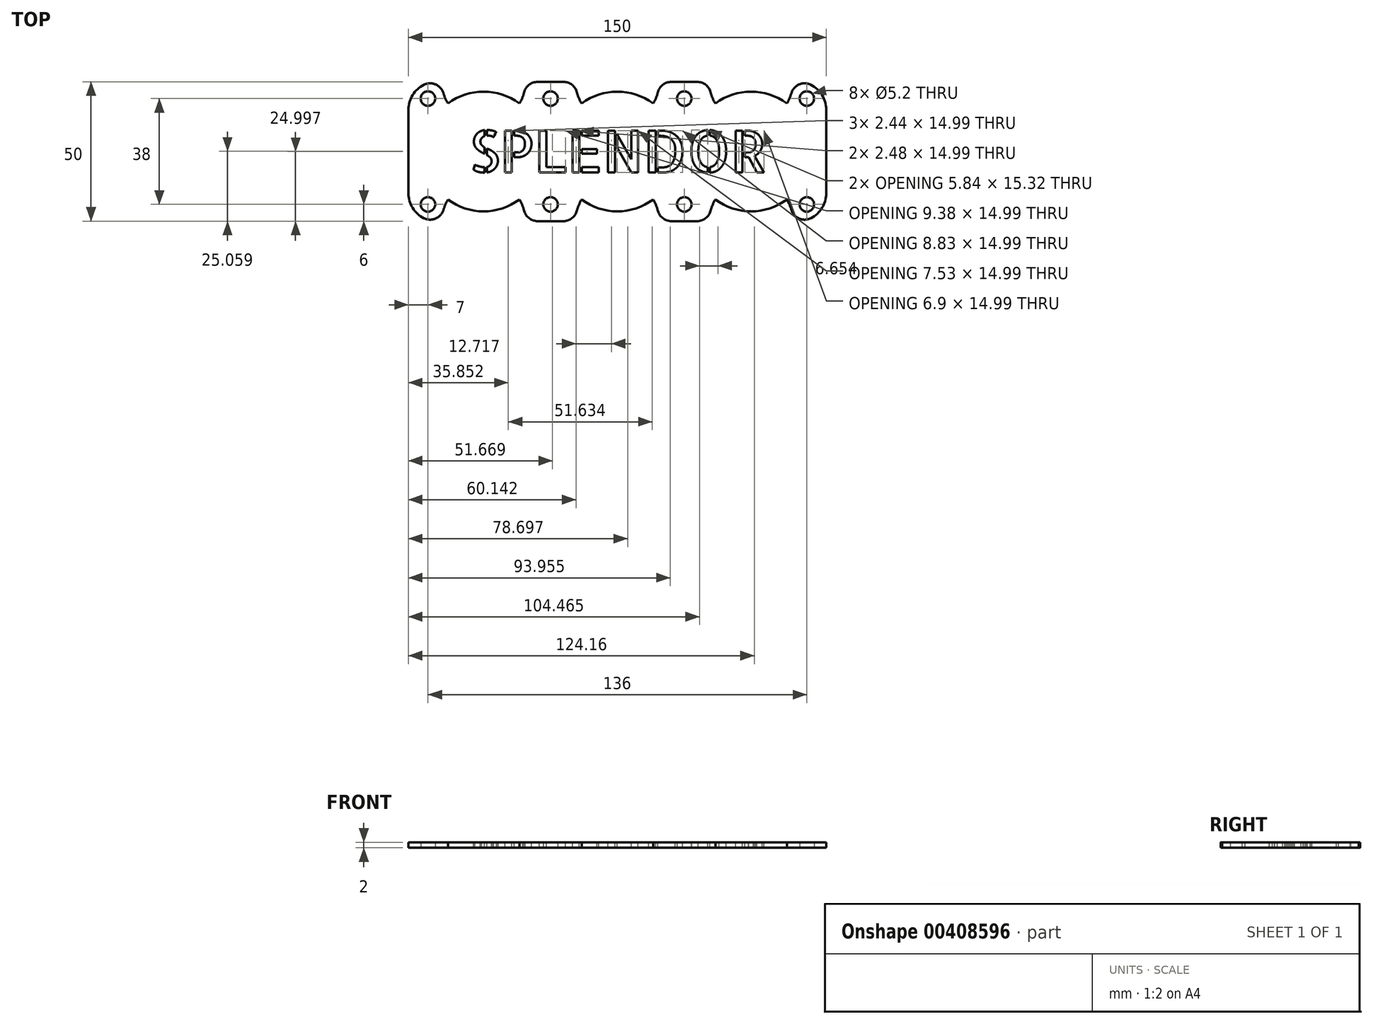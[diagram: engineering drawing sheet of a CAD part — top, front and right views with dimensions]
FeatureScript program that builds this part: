
annotation { "Feature Type Name" : "Feature", "Feature Type Description" : "" }
export const myFeature = defineFeature(function(context is Context, id is Id, definition is map)
    precondition{}
    {
        {
            var Q0;
            Q0=qCreatedBy(makeId("Top.planeOp"),FACE);
            var sketch = newSketch(context, id + "F0", { "sketchPlane" : qUnion([Q0])});
            skLineSegment(sketch, "E0.bottom", {"start": v(0, 0) * mm, "end": v(150, 0) * mm});
            skLineSegment(sketch, "E0.top", {"start": v(0, 50) * mm, "end": v(150, 50) * mm});
            skLineSegment(sketch, "E0.left", {"start": v(0, 0) * mm, "end": v(0, 50) * mm});
            skLineSegment(sketch, "E0.right", {"start": v(150, 0) * mm, "end": v(150, 50) * mm});
            skSolve(sketch);
        }
        {
            var Q0;
            Q0=makeQuery(id+"F0.imprint","IMPRINT",FACE,{"disambiguationData":[TD([[makeQuery(id+"F0.imprint","IMPRINT",EDGE,{"derivedFrom":sQuery(id+"F0.wireOp",EDGE,"E0.bottom")}),1.0]])]});
            var Q1;
            Q1=qSketchRegion(id+"F2",true);
            extrude(context, id + "F1", {"entities" : qUnion([Q0, Q1]), "depth" : 30 * mm});
        }
        {
            var Q0;
            Q0=makeQuery(id+"F1.opExtrude","CAP_FACE",FACE,{"disambiguationData":[OSD([sQuery(id+"F0.wireOp",EDGE,"E0.bottom"),sQuery(id+"F0.wireOp",EDGE,"E0.top"),sQuery(id+"F0.wireOp",EDGE,"E0.left"),sQuery(id+"F0.wireOp",EDGE,"E0.right")])],"isStart":false});
            var sketch = newSketch(context, id + "F2", { "sketchPlane" : qUnion([Q0])});
            skCircle(sketch, "E1", {"center": v(27, 25) * mm, "radius": 21.5 * mm});
            skCircle(sketch, "E2", {"center": v(75, 25) * mm, "radius": 21.5 * mm});
            skCircle(sketch, "E3", {"center": v(123, 25) * mm, "radius": 21.5 * mm});
            skSolve(sketch);
        }
        {
            var Q0;
            Q0=makeQuery(id+"F2.imprint","IMPRINT",FACE,{"disambiguationData":[TD([[makeQuery(id+"F2.imprint","IMPRINT",EDGE,{"derivedFrom":sQuery(id+"F2.wireOp",EDGE,"E2")}),1.0]])]});
            var Q1;
            Q1=makeQuery(id+"F2.imprint","IMPRINT",FACE,{"disambiguationData":[TD([[makeQuery(id+"F2.imprint","IMPRINT",EDGE,{"derivedFrom":sQuery(id+"F2.wireOp",EDGE,"E3")}),1.0]])]});
            var Q2;
            Q2=makeQuery(id+"F2.imprint","IMPRINT",FACE,{"disambiguationData":[TD([[makeQuery(id+"F2.imprint","IMPRINT",EDGE,{"derivedFrom":sQuery(id+"F2.wireOp",EDGE,"E1")}),1.0]])]});
            extrude(context, id + "F3", {"entities" : qUnion([Q0, Q1, Q2]), "operationType" : NewBodyOperationType.REMOVE, "oppositeDirection" : true, "depth" : 28 * mm});
        }
        {
            var Q0;
            Q0=makeQuery(id+"F1.opExtrude","CAP_FACE",FACE,{"disambiguationData":[OSD([sQuery(id+"F0.wireOp",EDGE,"E0.bottom"),sQuery(id+"F0.wireOp",EDGE,"E0.top"),sQuery(id+"F0.wireOp",EDGE,"E0.left"),sQuery(id+"F0.wireOp",EDGE,"E0.right")])],"isStart":false});
            var sketch = newSketch(context, id + "F4", { "sketchPlane" : qUnion([Q0])});
            skCircle(sketch, "E4", {"center": v(75, 50) * mm, "radius": 15 * mm});
            skCircle(sketch, "E5", {"center": v(123, 50) * mm, "radius": 15 * mm});
            skCircle(sketch, "E6", {"center": v(27, 50) * mm, "radius": 15 * mm});
            skCircle(sketch, "E7", {"center": v(27, 0) * mm, "radius": 15 * mm});
            skCircle(sketch, "E8", {"center": v(75, 0) * mm, "radius": 15 * mm});
            skCircle(sketch, "E9", {"center": v(123, 0) * mm, "radius": 15 * mm});
            skSolve(sketch);
        }
        {
            var Q0;
            {var subQ0=sQuery(id+"F4.wireOp",EDGE,"E4");var subQ1=makeQuery(id+"F1.opExtrude","CAP_EDGE",EDGE,{"disambiguationData":[OSD([sQuery(id+"F0.wireOp",EDGE,"E0.top")])],"isStart":false});var subQ2=makeQuery(id+"F4.imprint","INTERSECT",VERTEX,{"disambiguationData":[OD(0.0)],"derivedFrom":[subQ1,subQ0]});Q0=makeQuery(id+"F4.imprint","IMPRINT",FACE,{"disambiguationData":[TD([[makeQuery(id+"F4.imprint","IMPRINT",EDGE,{"disambiguationData":[TD([[subQ2,1.0]])],"derivedFrom":subQ0}),1.0]])]});}
            var Q1;
            {var subQ0=sQuery(id+"F4.wireOp",EDGE,"E5");var subQ1=makeQuery(id+"F1.opExtrude","CAP_EDGE",EDGE,{"disambiguationData":[OSD([sQuery(id+"F0.wireOp",EDGE,"E0.top")])],"isStart":false});var subQ2=makeQuery(id+"F4.imprint","INTERSECT",VERTEX,{"disambiguationData":[OD(0.0)],"derivedFrom":[subQ1,subQ0]});Q1=makeQuery(id+"F4.imprint","IMPRINT",FACE,{"disambiguationData":[TD([[makeQuery(id+"F4.imprint","IMPRINT",EDGE,{"disambiguationData":[TD([[subQ2,1.0]])],"derivedFrom":subQ0}),1.0]])]});}
            var Q2;
            {var subQ0=sQuery(id+"F4.wireOp",EDGE,"E7");var subQ1=makeQuery(id+"F1.opExtrude","CAP_EDGE",EDGE,{"disambiguationData":[OSD([sQuery(id+"F0.wireOp",EDGE,"E0.bottom")])],"isStart":false});var subQ2=makeQuery(id+"F4.imprint","INTERSECT",VERTEX,{"disambiguationData":[OD(0.0)],"derivedFrom":[subQ1,subQ0]});Q2=makeQuery(id+"F4.imprint","IMPRINT",FACE,{"disambiguationData":[TD([[makeQuery(id+"F4.imprint","IMPRINT",EDGE,{"disambiguationData":[TD([[subQ2,1.0]])],"derivedFrom":subQ0}),1.0]])]});}
            var Q3;
            {var subQ0=sQuery(id+"F4.wireOp",EDGE,"E8");var subQ1=makeQuery(id+"F1.opExtrude","CAP_EDGE",EDGE,{"disambiguationData":[OSD([sQuery(id+"F0.wireOp",EDGE,"E0.bottom")])],"isStart":false});var subQ2=makeQuery(id+"F4.imprint","INTERSECT",VERTEX,{"disambiguationData":[OD(0.0)],"derivedFrom":[subQ1,subQ0]});Q3=makeQuery(id+"F4.imprint","IMPRINT",FACE,{"disambiguationData":[TD([[makeQuery(id+"F4.imprint","IMPRINT",EDGE,{"disambiguationData":[TD([[subQ2,1.0]])],"derivedFrom":subQ0}),1.0]])]});}
            var Q4;
            {var subQ0=sQuery(id+"F4.wireOp",EDGE,"E9");var subQ1=makeQuery(id+"F1.opExtrude","CAP_EDGE",EDGE,{"disambiguationData":[OSD([sQuery(id+"F0.wireOp",EDGE,"E0.bottom")])],"isStart":false});var subQ2=makeQuery(id+"F4.imprint","INTERSECT",VERTEX,{"disambiguationData":[OD(0.0)],"derivedFrom":[subQ1,subQ0]});Q4=makeQuery(id+"F4.imprint","IMPRINT",FACE,{"disambiguationData":[TD([[makeQuery(id+"F4.imprint","IMPRINT",EDGE,{"disambiguationData":[TD([[subQ2,1.0]])],"derivedFrom":subQ0}),1.0]])]});}
            var Q5;
            {var subQ0=sQuery(id+"F4.wireOp",EDGE,"E4");var subQ1=makeQuery(id+"F3.boolean.opBoolean","COPY",EDGE,{"derivedFrom":makeQuery(id+"F3.opExtrude","CAP_EDGE",EDGE,{"disambiguationData":[OSD([sQuery(id+"F2.wireOp",EDGE,"E2")])],"isStart":true})});var subQ2=makeQuery(id+"F4.imprint","INTERSECT",VERTEX,{"disambiguationData":[OD(0.0)],"derivedFrom":[subQ1,subQ0]});Q5=makeQuery(id+"F4.imprint","IMPRINT",FACE,{"disambiguationData":[TD([[makeQuery(id+"F4.imprint","IMPRINT",EDGE,{"disambiguationData":[TD([[subQ2,-1.0]])],"derivedFrom":subQ0}),1.0]])]});}
            var Q6;
            {var subQ0=sQuery(id+"F4.wireOp",EDGE,"E5");var subQ1=makeQuery(id+"F3.boolean.opBoolean","COPY",EDGE,{"derivedFrom":makeQuery(id+"F3.opExtrude","CAP_EDGE",EDGE,{"disambiguationData":[OSD([sQuery(id+"F2.wireOp",EDGE,"E3")])],"isStart":true})});var subQ2=makeQuery(id+"F4.imprint","INTERSECT",VERTEX,{"disambiguationData":[OD(0.0)],"derivedFrom":[subQ1,subQ0]});Q6=makeQuery(id+"F4.imprint","IMPRINT",FACE,{"disambiguationData":[TD([[makeQuery(id+"F4.imprint","IMPRINT",EDGE,{"disambiguationData":[TD([[subQ2,-1.0]])],"derivedFrom":subQ0}),1.0]])]});}
            var Q7;
            {var subQ0=sQuery(id+"F4.wireOp",EDGE,"E6");var subQ1=makeQuery(id+"F3.boolean.opBoolean","COPY",EDGE,{"derivedFrom":makeQuery(id+"F3.opExtrude","CAP_EDGE",EDGE,{"disambiguationData":[OSD([sQuery(id+"F2.wireOp",EDGE,"E1")])],"isStart":true})});var subQ2=makeQuery(id+"F4.imprint","INTERSECT",VERTEX,{"disambiguationData":[OD(0.0)],"derivedFrom":[subQ1,subQ0]});Q7=makeQuery(id+"F4.imprint","IMPRINT",FACE,{"disambiguationData":[TD([[makeQuery(id+"F4.imprint","IMPRINT",EDGE,{"disambiguationData":[TD([[subQ2,-1.0]])],"derivedFrom":subQ0}),1.0]])]});}
            var Q8;
            {var subQ0=sQuery(id+"F4.wireOp",EDGE,"E7");var subQ1=makeQuery(id+"F3.boolean.opBoolean","COPY",EDGE,{"derivedFrom":makeQuery(id+"F3.opExtrude","CAP_EDGE",EDGE,{"disambiguationData":[OSD([sQuery(id+"F2.wireOp",EDGE,"E1")])],"isStart":true})});var subQ2=makeQuery(id+"F4.imprint","INTERSECT",VERTEX,{"disambiguationData":[OD(0.0)],"derivedFrom":[subQ1,subQ0]});Q8=makeQuery(id+"F4.imprint","IMPRINT",FACE,{"disambiguationData":[TD([[makeQuery(id+"F4.imprint","IMPRINT",EDGE,{"disambiguationData":[TD([[subQ2,-1.0]])],"derivedFrom":subQ0}),1.0]])]});}
            var Q9;
            {var subQ0=sQuery(id+"F4.wireOp",EDGE,"E8");var subQ1=makeQuery(id+"F3.boolean.opBoolean","COPY",EDGE,{"derivedFrom":makeQuery(id+"F3.opExtrude","CAP_EDGE",EDGE,{"disambiguationData":[OSD([sQuery(id+"F2.wireOp",EDGE,"E2")])],"isStart":true})});var subQ2=makeQuery(id+"F4.imprint","INTERSECT",VERTEX,{"disambiguationData":[OD(0.0)],"derivedFrom":[subQ1,subQ0]});Q9=makeQuery(id+"F4.imprint","IMPRINT",FACE,{"disambiguationData":[TD([[makeQuery(id+"F4.imprint","IMPRINT",EDGE,{"disambiguationData":[TD([[subQ2,-1.0]])],"derivedFrom":subQ0}),1.0]])]});}
            var Q10;
            {var subQ0=sQuery(id+"F4.wireOp",EDGE,"E9");var subQ1=makeQuery(id+"F3.boolean.opBoolean","COPY",EDGE,{"derivedFrom":makeQuery(id+"F3.opExtrude","CAP_EDGE",EDGE,{"disambiguationData":[OSD([sQuery(id+"F2.wireOp",EDGE,"E3")])],"isStart":true})});var subQ2=makeQuery(id+"F4.imprint","INTERSECT",VERTEX,{"disambiguationData":[OD(0.0)],"derivedFrom":[subQ1,subQ0]});Q10=makeQuery(id+"F4.imprint","IMPRINT",FACE,{"disambiguationData":[TD([[makeQuery(id+"F4.imprint","IMPRINT",EDGE,{"disambiguationData":[TD([[subQ2,-1.0]])],"derivedFrom":subQ0}),1.0]])]});}
            var Q11;
            {var subQ0=sQuery(id+"F4.wireOp",EDGE,"E4");var subQ1=makeQuery(id+"F1.opExtrude","CAP_EDGE",EDGE,{"disambiguationData":[OSD([sQuery(id+"F0.wireOp",EDGE,"E0.top")])],"isStart":false});var subQ2=makeQuery(id+"F4.imprint","INTERSECT",VERTEX,{"disambiguationData":[OD(0.0)],"derivedFrom":[subQ1,subQ0]});Q11=makeQuery(id+"F4.imprint","IMPRINT",FACE,{"disambiguationData":[TD([[makeQuery(id+"F4.imprint","IMPRINT",EDGE,{"disambiguationData":[TD([[subQ2,-1.0]])],"derivedFrom":subQ0}),1.0]])]});}
            var Q12;
            {var subQ0=sQuery(id+"F4.wireOp",EDGE,"E5");var subQ1=makeQuery(id+"F1.opExtrude","CAP_EDGE",EDGE,{"disambiguationData":[OSD([sQuery(id+"F0.wireOp",EDGE,"E0.top")])],"isStart":false});var subQ2=makeQuery(id+"F4.imprint","INTERSECT",VERTEX,{"disambiguationData":[OD(0.0)],"derivedFrom":[subQ1,subQ0]});Q12=makeQuery(id+"F4.imprint","IMPRINT",FACE,{"disambiguationData":[TD([[makeQuery(id+"F4.imprint","IMPRINT",EDGE,{"disambiguationData":[TD([[subQ2,-1.0]])],"derivedFrom":subQ0}),1.0]])]});}
            var Q13;
            {var subQ0=sQuery(id+"F4.wireOp",EDGE,"E6");var subQ1=makeQuery(id+"F1.opExtrude","CAP_EDGE",EDGE,{"disambiguationData":[OSD([sQuery(id+"F0.wireOp",EDGE,"E0.top")])],"isStart":false});var subQ2=makeQuery(id+"F4.imprint","INTERSECT",VERTEX,{"disambiguationData":[OD(0.0)],"derivedFrom":[subQ1,subQ0]});Q13=makeQuery(id+"F4.imprint","IMPRINT",FACE,{"disambiguationData":[TD([[makeQuery(id+"F4.imprint","IMPRINT",EDGE,{"disambiguationData":[TD([[subQ2,-1.0]])],"derivedFrom":subQ0}),1.0]])]});}
            var Q14;
            {var subQ0=sQuery(id+"F4.wireOp",EDGE,"E7");var subQ1=makeQuery(id+"F1.opExtrude","CAP_EDGE",EDGE,{"disambiguationData":[OSD([sQuery(id+"F0.wireOp",EDGE,"E0.bottom")])],"isStart":false});var subQ2=makeQuery(id+"F4.imprint","INTERSECT",VERTEX,{"disambiguationData":[OD(0.0)],"derivedFrom":[subQ1,subQ0]});Q14=makeQuery(id+"F4.imprint","IMPRINT",FACE,{"disambiguationData":[TD([[makeQuery(id+"F4.imprint","IMPRINT",EDGE,{"disambiguationData":[TD([[subQ2,-1.0]])],"derivedFrom":subQ0}),1.0]])]});}
            var Q15;
            {var subQ0=sQuery(id+"F4.wireOp",EDGE,"E8");var subQ1=makeQuery(id+"F1.opExtrude","CAP_EDGE",EDGE,{"disambiguationData":[OSD([sQuery(id+"F0.wireOp",EDGE,"E0.bottom")])],"isStart":false});var subQ2=makeQuery(id+"F4.imprint","INTERSECT",VERTEX,{"disambiguationData":[OD(0.0)],"derivedFrom":[subQ1,subQ0]});Q15=makeQuery(id+"F4.imprint","IMPRINT",FACE,{"disambiguationData":[TD([[makeQuery(id+"F4.imprint","IMPRINT",EDGE,{"disambiguationData":[TD([[subQ2,-1.0]])],"derivedFrom":subQ0}),1.0]])]});}
            var Q16;
            {var subQ0=sQuery(id+"F4.wireOp",EDGE,"E9");var subQ1=makeQuery(id+"F1.opExtrude","CAP_EDGE",EDGE,{"disambiguationData":[OSD([sQuery(id+"F0.wireOp",EDGE,"E0.bottom")])],"isStart":false});var subQ2=makeQuery(id+"F4.imprint","INTERSECT",VERTEX,{"disambiguationData":[OD(0.0)],"derivedFrom":[subQ1,subQ0]});Q16=makeQuery(id+"F4.imprint","IMPRINT",FACE,{"disambiguationData":[TD([[makeQuery(id+"F4.imprint","IMPRINT",EDGE,{"disambiguationData":[TD([[subQ2,-1.0]])],"derivedFrom":subQ0}),1.0]])]});}
            extrude(context, id + "F5", {"entities" : qUnion([Q0, Q1, Q2, Q3, Q4, Q5, Q6, Q7, Q8, Q9, Q10, Q11, Q12, Q13, Q14, Q15, Q16]), "operationType" : NewBodyOperationType.REMOVE, "endBound" : BoundingType.THROUGH_ALL, "oppositeDirection" : true, "depth" : 25 * mm});
        }
        {
            var Q0;
            Q0=makeQuery(id+"F1.opExtrude","SWEPT_EDGE",EDGE,{"disambiguationData":[OSD([sQuery(id+"F0.wireOp",EDGE,"E0.bottom"),sQuery(id+"F0.wireOp",EDGE,"E0.right")])]});
            fillet(context, id + "F6", {"entities" : qUnion([Q0]), "radius" : 10 * mm, "tangentPropagation" : true, "allowEdgeOverflow" : false});
        }
        {
            var Q0;
            Q0=makeQuery(id+"F1.opExtrude","SWEPT_EDGE",EDGE,{"disambiguationData":[OSD([sQuery(id+"F0.wireOp",EDGE,"E0.top"),sQuery(id+"F0.wireOp",EDGE,"E0.right")])]});
            var Q1;
            Q1=makeQuery(id+"F1.opExtrude","SWEPT_EDGE",EDGE,{"disambiguationData":[OSD([sQuery(id+"F0.wireOp",EDGE,"E0.bottom"),sQuery(id+"F0.wireOp",EDGE,"E0.left")])]});
            var Q2;
            Q2=makeQuery(id+"F1.opExtrude","SWEPT_EDGE",EDGE,{"disambiguationData":[OSD([sQuery(id+"F0.wireOp",EDGE,"E0.top"),sQuery(id+"F0.wireOp",EDGE,"E0.left")])]});
            fillet(context, id + "F7", {"entities" : qUnion([Q0, Q1, Q2]), "radius" : 10 * mm, "tangentPropagation" : true, "allowEdgeOverflow" : false});
        }
        {
            var Q0;
            Q0=makeQuery(id+"F5.boolean.opBoolean","INTERSECT",EDGE,{"disambiguationData":[OD(0.0)],"derivedFrom":[makeQuery(id+"F1.opExtrude","SWEPT_FACE",FACE,{"disambiguationData":[OSD([sQuery(id+"F0.wireOp",EDGE,"E0.bottom")])]}),makeQuery(id+"F5.opExtrude","SWEPT_FACE",FACE,{"disambiguationData":[OSD([sQuery(id+"F4.wireOp",EDGE,"E7")])]})]});
            var Q1;
            {var subQ0=sQuery(id+"F4.wireOp",EDGE,"E6");var subQ1=sQuery(id+"F0.wireOp",EDGE,"E0.top");Q1=makeQuery(id+"F5.boolean.opBoolean","COPY",EDGE,{"derivedFrom":makeQuery(id+"F5.opExtrude","SWEPT_EDGE",EDGE,{"disambiguationData":[OSD([subQ1,subQ0]),TDD([makeQuery(id+"F4.imprint","INTERSECT",VERTEX,{"disambiguationData":[OD(0.0)],"derivedFrom":[makeQuery(id+"F1.opExtrude","CAP_EDGE",EDGE,{"disambiguationData":[OSD([subQ1])],"isStart":false}),subQ0]})])]})});}
            var Q2;
            Q2=makeQuery(id+"F5.boolean.opBoolean","INTERSECT",EDGE,{"disambiguationData":[OD(0.0)],"derivedFrom":[makeQuery(id+"F1.opExtrude","SWEPT_FACE",FACE,{"disambiguationData":[OSD([sQuery(id+"F0.wireOp",EDGE,"E0.top")])]}),makeQuery(id+"F5.opExtrude","SWEPT_FACE",FACE,{"disambiguationData":[OSD([sQuery(id+"F4.wireOp",EDGE,"E4")])]})]});
            var Q3;
            Q3=makeQuery(id+"F5.boolean.opBoolean","INTERSECT",EDGE,{"disambiguationData":[OD(1.0)],"derivedFrom":[makeQuery(id+"F1.opExtrude","SWEPT_FACE",FACE,{"disambiguationData":[OSD([sQuery(id+"F0.wireOp",EDGE,"E0.top")])]}),makeQuery(id+"F5.opExtrude","SWEPT_FACE",FACE,{"disambiguationData":[OSD([sQuery(id+"F4.wireOp",EDGE,"E5")])]})]});
            var Q4;
            Q4=makeQuery(id+"F5.boolean.opBoolean","INTERSECT",EDGE,{"disambiguationData":[OD(1.0)],"derivedFrom":[makeQuery(id+"F1.opExtrude","SWEPT_FACE",FACE,{"disambiguationData":[OSD([sQuery(id+"F0.wireOp",EDGE,"E0.bottom")])]}),makeQuery(id+"F5.opExtrude","SWEPT_FACE",FACE,{"disambiguationData":[OSD([sQuery(id+"F4.wireOp",EDGE,"E9")])]})]});
            var Q5;
            Q5=makeQuery(id+"F5.boolean.opBoolean","INTERSECT",EDGE,{"disambiguationData":[OD(1.0)],"derivedFrom":[makeQuery(id+"F1.opExtrude","SWEPT_FACE",FACE,{"disambiguationData":[OSD([sQuery(id+"F0.wireOp",EDGE,"E0.bottom")])]}),makeQuery(id+"F5.opExtrude","SWEPT_FACE",FACE,{"disambiguationData":[OSD([sQuery(id+"F4.wireOp",EDGE,"E8")])]})]});
            var Q6;
            Q6=makeQuery(id+"F5.boolean.opBoolean","INTERSECT",EDGE,{"disambiguationData":[OD(1.0)],"derivedFrom":[makeQuery(id+"F1.opExtrude","SWEPT_FACE",FACE,{"disambiguationData":[OSD([sQuery(id+"F0.wireOp",EDGE,"E0.bottom")])]}),makeQuery(id+"F5.opExtrude","SWEPT_FACE",FACE,{"disambiguationData":[OSD([sQuery(id+"F4.wireOp",EDGE,"E7")])]})]});
            var Q7;
            Q7=makeQuery(id+"F5.boolean.opBoolean","INTERSECT",EDGE,{"disambiguationData":[OD(0.0)],"derivedFrom":[makeQuery(id+"F1.opExtrude","SWEPT_FACE",FACE,{"disambiguationData":[OSD([sQuery(id+"F0.wireOp",EDGE,"E0.bottom")])]}),makeQuery(id+"F5.opExtrude","SWEPT_FACE",FACE,{"disambiguationData":[OSD([sQuery(id+"F4.wireOp",EDGE,"E8")])]})]});
            var Q8;
            Q8=makeQuery(id+"F5.boolean.opBoolean","INTERSECT",EDGE,{"disambiguationData":[OD(0.0)],"derivedFrom":[makeQuery(id+"F1.opExtrude","SWEPT_FACE",FACE,{"disambiguationData":[OSD([sQuery(id+"F0.wireOp",EDGE,"E0.bottom")])]}),makeQuery(id+"F5.opExtrude","SWEPT_FACE",FACE,{"disambiguationData":[OSD([sQuery(id+"F4.wireOp",EDGE,"E9")])]})]});
            var Q9;
            {var subQ0=sQuery(id+"F4.wireOp",EDGE,"E6");var subQ1=sQuery(id+"F0.wireOp",EDGE,"E0.top");Q9=makeQuery(id+"F5.boolean.opBoolean","COPY",EDGE,{"derivedFrom":makeQuery(id+"F5.opExtrude","SWEPT_EDGE",EDGE,{"disambiguationData":[OSD([subQ1,subQ0]),TDD([makeQuery(id+"F4.imprint","INTERSECT",VERTEX,{"disambiguationData":[OD(1.0)],"derivedFrom":[makeQuery(id+"F1.opExtrude","CAP_EDGE",EDGE,{"disambiguationData":[OSD([subQ1])],"isStart":false}),subQ0]})])]})});}
            var Q10;
            Q10=makeQuery(id+"F5.boolean.opBoolean","INTERSECT",EDGE,{"disambiguationData":[OD(1.0)],"derivedFrom":[makeQuery(id+"F1.opExtrude","SWEPT_FACE",FACE,{"disambiguationData":[OSD([sQuery(id+"F0.wireOp",EDGE,"E0.top")])]}),makeQuery(id+"F5.opExtrude","SWEPT_FACE",FACE,{"disambiguationData":[OSD([sQuery(id+"F4.wireOp",EDGE,"E4")])]})]});
            var Q11;
            Q11=makeQuery(id+"F5.boolean.opBoolean","INTERSECT",EDGE,{"disambiguationData":[OD(0.0)],"derivedFrom":[makeQuery(id+"F1.opExtrude","SWEPT_FACE",FACE,{"disambiguationData":[OSD([sQuery(id+"F0.wireOp",EDGE,"E0.top")])]}),makeQuery(id+"F5.opExtrude","SWEPT_FACE",FACE,{"disambiguationData":[OSD([sQuery(id+"F4.wireOp",EDGE,"E5")])]})]});
            fillet(context, id + "F8", {"entities" : qUnion([Q0, Q1, Q2, Q3, Q4, Q5, Q6, Q7, Q8, Q9, Q10, Q11]), "radius" : 5 * mm, "tangentPropagation" : true, "allowEdgeOverflow" : false});
        }
        {
            var Q0;
            Q0=makeQuery(id+"F1.opExtrude","CAP_FACE",FACE,{"disambiguationData":[OSD([sQuery(id+"F0.wireOp",EDGE,"E0.bottom"),sQuery(id+"F0.wireOp",EDGE,"E0.top"),sQuery(id+"F0.wireOp",EDGE,"E0.left"),sQuery(id+"F0.wireOp",EDGE,"E0.right")])],"isStart":true});
            var sketch = newSketch(context, id + "F9", { "sketchPlane" : qUnion([Q0])});
            skCircle(sketch, "E10", {"center": v(7, -6) * mm, "radius": 2.6 * mm});
            skCircle(sketch, "E11", {"center": v(51, -6) * mm, "radius": 2.6 * mm});
            skPoint(sketch, "E12.centerSnap0", {"position": v(126.78, -7.26) * mm});
            skCircle(sketch, "E13", {"center": v(143, -6) * mm, "radius": 2.6 * mm});
            skCircle(sketch, "E14", {"center": v(7, -44) * mm, "radius": 2.6 * mm});
            skCircle(sketch, "E15", {"center": v(51, -44) * mm, "radius": 2.6 * mm});
            skCircle(sketch, "E16", {"center": v(99, -44) * mm, "radius": 2.6 * mm});
            skCircle(sketch, "E17", {"center": v(143, -44) * mm, "radius": 2.6 * mm});
            skCircle(sketch, "E18", {"center": v(99, -6) * mm, "radius": 2.6 * mm});
            skSolve(sketch);
        }
        {
            var Q0;
            Q0=makeQuery(id+"F9.imprint","IMPRINT",FACE,{"disambiguationData":[TD([[makeQuery(id+"F9.imprint","IMPRINT",EDGE,{"derivedFrom":sQuery(id+"F9.wireOp",EDGE,"E10")}),1.0]])]});
            var Q1;
            Q1=makeQuery(id+"F9.imprint","IMPRINT",FACE,{"disambiguationData":[TD([[makeQuery(id+"F9.imprint","IMPRINT",EDGE,{"derivedFrom":sQuery(id+"F9.wireOp",EDGE,"E11")}),1.0]])]});
            var Q2;
            Q2=makeQuery(id+"F9.imprint","IMPRINT",FACE,{"disambiguationData":[TD([[makeQuery(id+"F9.imprint","IMPRINT",EDGE,{"derivedFrom":sQuery(id+"F9.wireOp",EDGE,"E13")}),1.0]])]});
            var Q3;
            Q3=makeQuery(id+"F9.imprint","IMPRINT",FACE,{"disambiguationData":[TD([[makeQuery(id+"F9.imprint","IMPRINT",EDGE,{"derivedFrom":sQuery(id+"F9.wireOp",EDGE,"E14")}),1.0]])]});
            var Q4;
            Q4=makeQuery(id+"F9.imprint","IMPRINT",FACE,{"disambiguationData":[TD([[makeQuery(id+"F9.imprint","IMPRINT",EDGE,{"derivedFrom":sQuery(id+"F9.wireOp",EDGE,"E15")}),1.0]])]});
            var Q5;
            Q5=makeQuery(id+"F9.imprint","IMPRINT",FACE,{"disambiguationData":[TD([[makeQuery(id+"F9.imprint","IMPRINT",EDGE,{"derivedFrom":sQuery(id+"F9.wireOp",EDGE,"E16")}),1.0]])]});
            var Q6;
            Q6=makeQuery(id+"F9.imprint","IMPRINT",FACE,{"disambiguationData":[TD([[makeQuery(id+"F9.imprint","IMPRINT",EDGE,{"derivedFrom":sQuery(id+"F9.wireOp",EDGE,"E18")}),1.0]])]});
            var Q7;
            Q7=makeQuery(id+"F9.imprint","IMPRINT",FACE,{"disambiguationData":[TD([[makeQuery(id+"F9.imprint","IMPRINT",EDGE,{"derivedFrom":sQuery(id+"F9.wireOp",EDGE,"E17")}),1.0]])]});
            extrude(context, id + "F10", {"entities" : qUnion([Q0, Q1, Q2, Q3, Q4, Q5, Q6, Q7]), "operationType" : NewBodyOperationType.REMOVE, "oppositeDirection" : true, "depth" : 10 * mm});
        }
        {
            var Q0;
            {var subQ0=sQuery(id+"F0.wireOp",EDGE,"E0.bottom");var subQ1=sQuery(id+"F0.wireOp",EDGE,"E0.top");Q0=makeQuery(id+"F5.boolean.opBoolean","SPLIT",FACE,{"disambiguationData":[TD([makeQuery(id+"F1.opExtrude","SWEPT_FACE",FACE,{"disambiguationData":[OSD([subQ0])]}),makeQuery(id+"F1.opExtrude","SWEPT_FACE",FACE,{"disambiguationData":[OSD([subQ1])]}),makeQuery(id+"F3.boolean.opBoolean","COPY",FACE,{"derivedFrom":makeQuery(id+"F3.opExtrude","SWEPT_FACE",FACE,{"disambiguationData":[OSD([sQuery(id+"F2.wireOp",EDGE,"E1")])]})}),makeQuery(id+"F3.boolean.opBoolean","COPY",FACE,{"derivedFrom":makeQuery(id+"F3.opExtrude","SWEPT_FACE",FACE,{"disambiguationData":[OSD([sQuery(id+"F2.wireOp",EDGE,"E2")])]})}),makeQuery(id+"F5.opExtrude","SWEPT_FACE",FACE,{"disambiguationData":[OSD([sQuery(id+"F4.wireOp",EDGE,"E4")])]}),makeQuery(id+"F5.opExtrude","SWEPT_FACE",FACE,{"disambiguationData":[OSD([sQuery(id+"F4.wireOp",EDGE,"E6")])]}),makeQuery(id+"F5.opExtrude","SWEPT_FACE",FACE,{"disambiguationData":[OSD([sQuery(id+"F4.wireOp",EDGE,"E7")])]}),makeQuery(id+"F5.opExtrude","SWEPT_FACE",FACE,{"disambiguationData":[OSD([sQuery(id+"F4.wireOp",EDGE,"E8")])]})])],"derivedFrom":makeQuery(id+"F1.opExtrude","CAP_FACE",FACE,{"disambiguationData":[OSD([subQ0,subQ1,sQuery(id+"F0.wireOp",EDGE,"E0.left"),sQuery(id+"F0.wireOp",EDGE,"E0.right")])],"isStart":false})});}
            var sketch = newSketch(context, id + "F11", { "sketchPlane" : qUnion([Q0])});
            skLineSegment(sketch, "E19.bottom", {"start": v(-18.88, -14.91) * mm, "end": v(184.1, -14.91) * mm});
            skLineSegment(sketch, "E19.top", {"start": v(-18.88, 62.8) * mm, "end": v(184.1, 62.8) * mm});
            skLineSegment(sketch, "E19.left", {"start": v(-18.88, -14.91) * mm, "end": v(-18.88, 62.8) * mm});
            skLineSegment(sketch, "E19.right", {"start": v(184.1, -14.91) * mm, "end": v(184.1, 62.8) * mm});
            skSolve(sketch);
        }
        {
            var Q0;
            Q0 = qSketchRegion(id + "F11", true);
            extrude(context, id + "F12", {"entities" : qUnion([Q0]), "operationType" : NewBodyOperationType.REMOVE, "oppositeDirection" : true, "depth" : 28 * mm});
        }
        {
            var Q0;
            Q0=makeQuery(id+"F12.boolean.opBoolean","MERGE",FACE,{"derivedFrom":[makeQuery(id+"F3.boolean.opBoolean","COPY",FACE,{"derivedFrom":makeQuery(id+"F3.opExtrude","CAP_FACE",FACE,{"disambiguationData":[OSD([sQuery(id+"F2.wireOp",EDGE,"E1")])],"isStart":false})}),makeQuery(id+"F3.boolean.opBoolean","COPY",FACE,{"derivedFrom":makeQuery(id+"F3.opExtrude","CAP_FACE",FACE,{"disambiguationData":[OSD([sQuery(id+"F2.wireOp",EDGE,"E2")])],"isStart":false})}),makeQuery(id+"F3.boolean.opBoolean","COPY",FACE,{"derivedFrom":makeQuery(id+"F3.opExtrude","CAP_FACE",FACE,{"disambiguationData":[OSD([sQuery(id+"F2.wireOp",EDGE,"E3")])],"isStart":false})}),makeQuery(id+"F12.opExtrude","CAP_FACE",FACE,{"disambiguationData":[OSD([sQuery(id+"F11.wireOp",EDGE,"E19.bottom"),sQuery(id+"F11.wireOp",EDGE,"E19.top"),sQuery(id+"F11.wireOp",EDGE,"E19.left"),sQuery(id+"F11.wireOp",EDGE,"E19.right")])],"isStart":false})]});
            var sketch = newSketch(context, id + "F13", { "sketchPlane" : qUnion([Q0])});
            skText(sketch, "E20", { "text": "SPLENDOR", "fontName": "AllertaStencil-Regular.ttf"});
            const initialGuessF13  = {"E20": [0.02175, 0.0175, 1, 0, 0.015]};
            skSetInitialGuess(sketch, initialGuessF13);
            skSolve(sketch);
        }
        {
            var Q0;
            Q0 = qSketchRegion(id + "F13", true);
            extrude(context, id + "F14", {"entities" : qUnion([Q0]), "operationType" : NewBodyOperationType.REMOVE, "endBound" : BoundingType.THROUGH_ALL, "oppositeDirection" : true, "depth" : 25 * mm});
        }
    });
